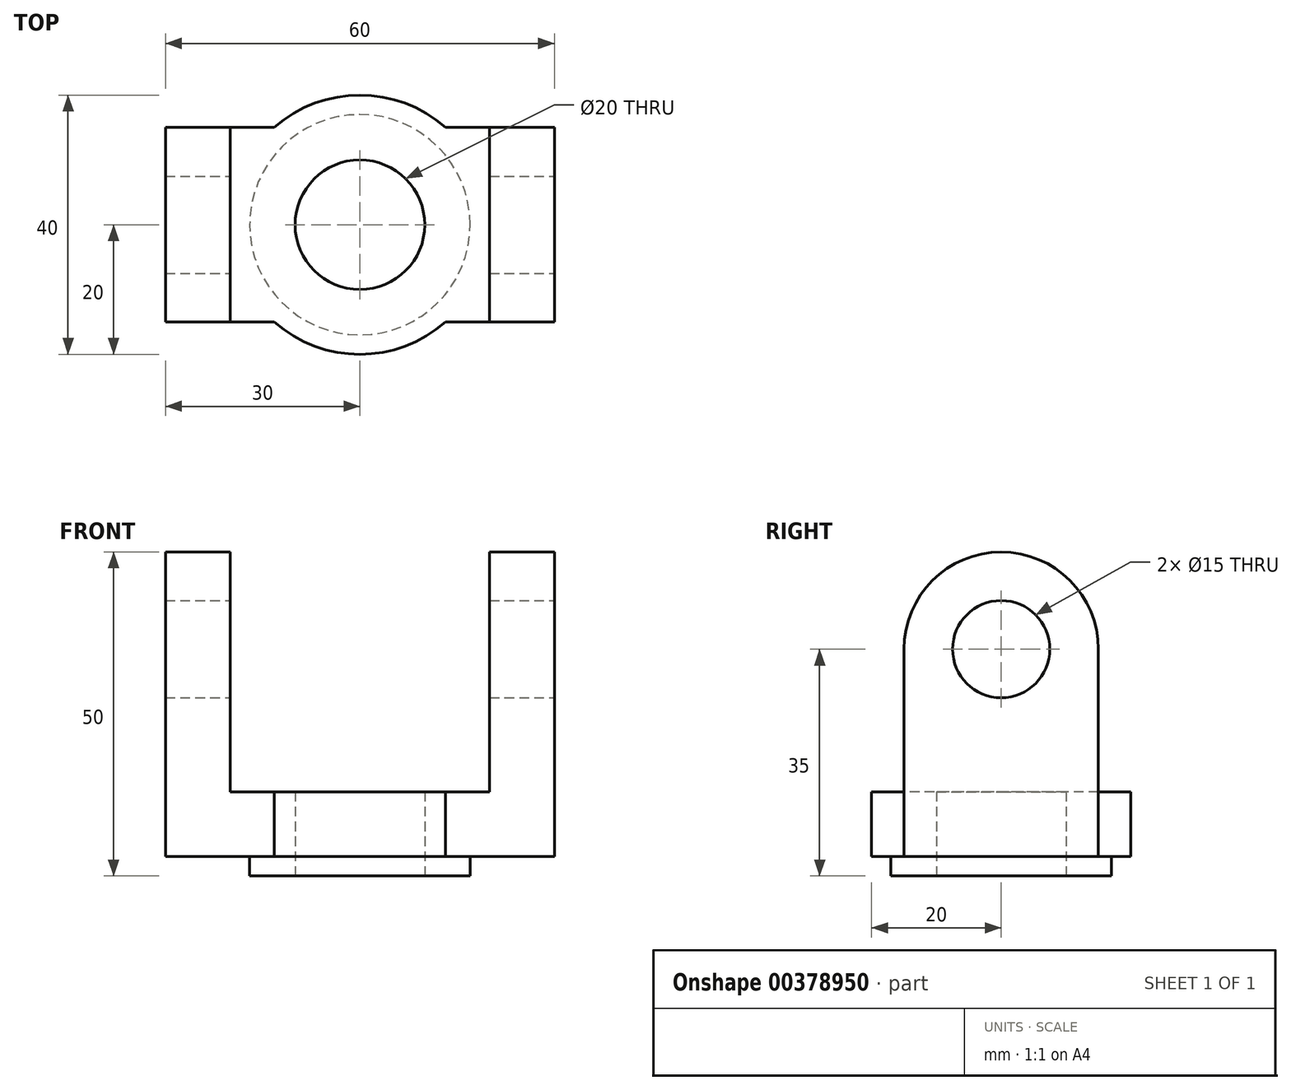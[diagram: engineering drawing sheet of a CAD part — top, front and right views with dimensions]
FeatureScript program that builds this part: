
annotation { "Feature Type Name" : "Feature", "Feature Type Description" : "" }
export const myFeature = defineFeature(function(context is Context, id is Id, definition is map)
    precondition{}
    {
        {
            var Q0;
            Q0=qCreatedBy(makeId("Top.planeOp"),FACE);
            var sketch = newSketch(context, id + "F0", { "sketchPlane" : qUnion([Q0])});
            skCircle(sketch, "E0", {"center": v(0, 0) * mm, "radius": 20 * mm});
            skLineSegment(sketch, "E1", {"start": v(13.23, 15) * mm, "end": v(30, 15) * mm});
            skLineSegment(sketch, "E2", {"start": v(30, 15) * mm, "end": v(30, -15) * mm});
            skLineSegment(sketch, "E3", {"start": v(30, -15) * mm, "end": v(13.23, -15) * mm});
            skLineSegment(sketch, "E4", {"start": v(-13.23, 15) * mm, "end": v(-30, 15) * mm});
            skLineSegment(sketch, "E5", {"start": v(-30, 15) * mm, "end": v(-30, -15) * mm});
            skLineSegment(sketch, "E6", {"start": v(-30, -15) * mm, "end": v(-13.23, -15) * mm});
            skCircle(sketch, "E7", {"center": v(0, 0) * mm, "radius": 10 * mm});
            skLineSegment(sketch, "E8", {"start": v(-20, 15) * mm, "end": v(-20, -15) * mm});
            skLineSegment(sketch, "E9", {"start": v(20, 15) * mm, "end": v(20, -15) * mm});
            skSolve(sketch);
        }
        {
            var Q0;
            Q0=makeQuery(id+"F0.imprint","IMPRINT",FACE,{"disambiguationData":[TD([[makeQuery(id+"F0.imprint","IMPRINT",EDGE,{"derivedFrom":sQuery(id+"F0.wireOp",EDGE,"E7")}),-1.0]])]});
            var Q1;
            {var subQ0=sQuery(id+"F0.wireOp",EDGE,"E1");var subQ1=sQuery(id+"F0.wireOp",EDGE,"E0");var subQ2=makeQuery(id+"F0.imprint","INTERSECT",VERTEX,{"derivedFrom":[subQ1,subQ0]});Q1=makeQuery(id+"F0.imprint","IMPRINT",FACE,{"disambiguationData":[TD([[makeQuery(id+"F0.imprint","IMPRINT",EDGE,{"disambiguationData":[TD([[subQ2,1.0]])],"derivedFrom":subQ1}),-1.0]])]});}
            var Q2;
            {var subQ0=sQuery(id+"F0.wireOp",EDGE,"E3");var subQ1=sQuery(id+"F0.wireOp",EDGE,"E0");var subQ2=makeQuery(id+"F0.imprint","INTERSECT",VERTEX,{"derivedFrom":[subQ1,subQ0]});Q2=makeQuery(id+"F0.imprint","IMPRINT",FACE,{"disambiguationData":[TD([[makeQuery(id+"F0.imprint","IMPRINT",EDGE,{"disambiguationData":[TD([[subQ2,-1.0]])],"derivedFrom":subQ1}),-1.0]])]});}
            var Q3;
            {var subQ0=sQuery(id+"F0.wireOp",EDGE,"E6");var subQ1=sQuery(id+"F0.wireOp",EDGE,"E0");var subQ2=makeQuery(id+"F0.imprint","INTERSECT",VERTEX,{"derivedFrom":[subQ1,subQ0]});Q3=makeQuery(id+"F0.imprint","IMPRINT",FACE,{"disambiguationData":[TD([[makeQuery(id+"F0.imprint","IMPRINT",EDGE,{"disambiguationData":[TD([[subQ2,1.0]])],"derivedFrom":subQ1}),-1.0]])]});}
            var Q4;
            {var subQ0=sQuery(id+"F0.wireOp",EDGE,"E4");var subQ1=sQuery(id+"F0.wireOp",EDGE,"E0");var subQ2=makeQuery(id+"F0.imprint","INTERSECT",VERTEX,{"derivedFrom":[subQ1,subQ0]});Q4=makeQuery(id+"F0.imprint","IMPRINT",FACE,{"disambiguationData":[TD([[makeQuery(id+"F0.imprint","IMPRINT",EDGE,{"disambiguationData":[TD([[subQ2,-1.0]])],"derivedFrom":subQ1}),-1.0]])]});}
            extrude(context, id + "F1", {"entities" : qUnion([Q0, Q1, Q2, Q3, Q4]), "depth" : 10 * mm});
        }
        {
            var Q0;
            {var subQ4=sQuery(id+"F0.wireOp",EDGE,"E2");Q0=makeQuery(id+"F0.imprint","IMPRINT",FACE,{"disambiguationData":[TD([[makeQuery(id+"F0.imprint","IMPRINT",EDGE,{"derivedFrom":subQ4}),-1.0]])]});}
            var Q1;
            {var subQ1=sQuery(id+"F0.wireOp",EDGE,"E5");Q1=makeQuery(id+"F0.imprint","IMPRINT",FACE,{"disambiguationData":[TD([[makeQuery(id+"F0.imprint","IMPRINT",EDGE,{"derivedFrom":subQ1}),1.0]])]});}
            extrude(context, id + "F2", {"entities" : qUnion([Q0, Q1]), "operationType" : NewBodyOperationType.ADD, "depth" : (9.5 * 5) * mm});
        }
        {
            var Q0;
            Q0=makeQuery(id+"F2.opExtrude","SWEPT_FACE",FACE,{"disambiguationData":[OSD([sQuery(id+"F0.wireOp",EDGE,"E2")])]});
            var sketch = newSketch(context, id + "F3", { "sketchPlane" : qUnion([Q0])});
            skLineSegment(sketch, "E10", {"start": v(-15, 47.5) * mm, "end": v(15, 47.5) * mm});
            skLineSegment(sketch, "E11", {"start": v(15, 47.5) * mm, "end": v(15, 0) * mm});
            skLineSegment(sketch, "E12", {"start": v(15, 0) * mm, "end": v(-15, 0) * mm});
            skLineSegment(sketch, "E13", {"start": v(-15, 0) * mm, "end": v(-15, 47.5) * mm});
            skCircle(sketch, "E14", {"center": v(0, 32) * mm, "radius": 7.5 * mm});
            skArc(sketch, "E15", {"start": v(15, 32) * mm, "mid": v(0, 47) * mm, "end": v(-15, 32) * mm});
            skSolve(sketch);
        }
        {
            var Q0;
            {var subQ0=sQuery(id+"F3.wireOp",EDGE,"E10");Q0=makeQuery(id+"F3.imprint","IMPRINT",FACE,{"disambiguationData":[TD([[makeQuery(id+"F3.imprint","IMPRINT",EDGE,{"derivedFrom":subQ0}),1.0]])]});}
            var Q1;
            Q1=makeQuery(id+"F3.imprint","IMPRINT",FACE,{"disambiguationData":[TD([[makeQuery(id+"F3.imprint","IMPRINT",EDGE,{"derivedFrom":sQuery(id+"F3.wireOp",EDGE,"E14")}),1.0]])]});
            extrude(context, id + "F4", {"entities" : qUnion([Q0, Q1]), "operationType" : NewBodyOperationType.REMOVE, "endBound" : BoundingType.THROUGH_ALL, "oppositeDirection" : true, "depth" : 25 * mm});
        }
        {
            var Q0;
            Q0=makeQuery(id+"F0.imprint","IMPRINT",FACE,{"disambiguationData":[TD([[makeQuery(id+"F0.imprint","IMPRINT",EDGE,{"derivedFrom":sQuery(id+"F0.wireOp",EDGE,"E7")}),-1.0]])]});
            var sketch = newSketch(context, id + "F5", { "sketchPlane" : qUnion([Q0])});
            skCircle(sketch, "E16", {"center": v(0, 0) * mm, "radius": 17 * mm});
            skCircle(sketch, "E17", {"center": v(0, 0) * mm, "radius": 10 * mm});
            skSolve(sketch);
        }
        {
            var Q0;
            Q0=makeQuery(id+"F5.imprint","IMPRINT",FACE,{"disambiguationData":[TD([[makeQuery(id+"F5.imprint","IMPRINT",EDGE,{"derivedFrom":sQuery(id+"F5.wireOp",EDGE,"E16")}),1.0]])]});
            extrude(context, id + "F6", {"entities" : qUnion([Q0]), "operationType" : NewBodyOperationType.ADD, "oppositeDirection" : true, "depth" : 3 * mm});
        }
    });
